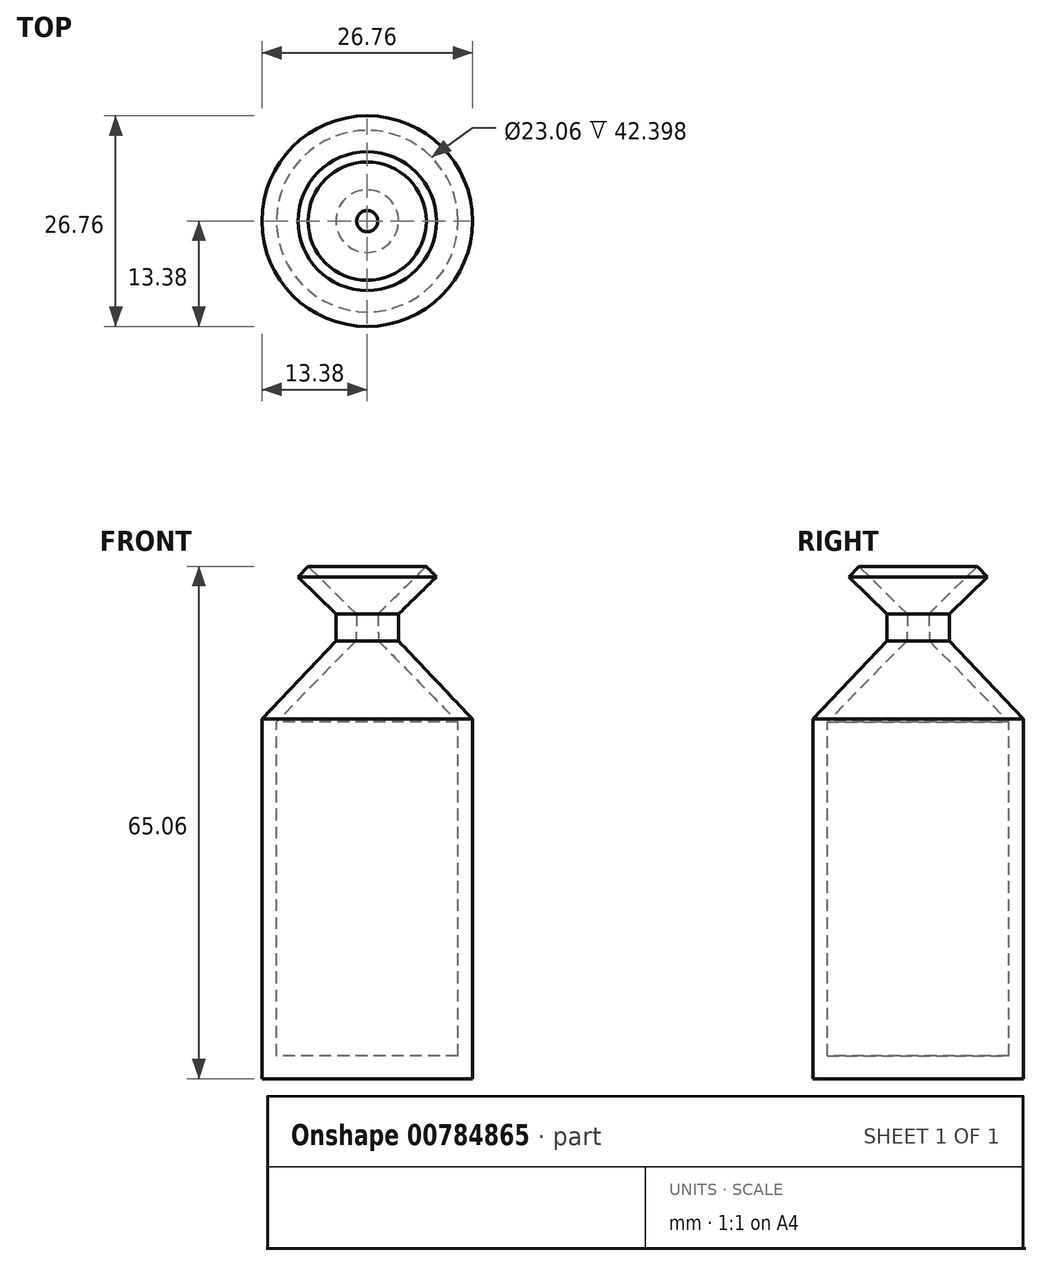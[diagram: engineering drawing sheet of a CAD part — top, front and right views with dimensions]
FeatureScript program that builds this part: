
annotation { "Feature Type Name" : "Feature", "Feature Type Description" : "" }
export const myFeature = defineFeature(function(context is Context, id is Id, definition is map)
    precondition{}
    {
        {
            var Q0;
            Q0=qCreatedBy(makeId("Front.planeOp"),FACE);
            var sketch = newSketch(context, id + "F0", { "sketchPlane" : qUnion([Q0])});
            skLineSegment(sketch, "E0", {"start": v(0, 0) * mm, "end": v(13.38, 0) * mm});
            skLineSegment(sketch, "E1", {"start": v(13.38, 0) * mm, "end": v(13.38, 45.67) * mm});
            skLineSegment(sketch, "E2", {"start": v(13.38, 45.67) * mm, "end": v(3.98, 55.62) * mm});
            skLineSegment(sketch, "E3", {"start": v(3.98, 55.62) * mm, "end": v(3.98, 59.03) * mm});
            skLineSegment(sketch, "E4", {"start": v(3.98, 59.03) * mm, "end": v(8.8, 63.74) * mm});
            skLineSegment(sketch, "E5", {"start": v(8.8, 63.74) * mm, "end": v(7.5, 65.06) * mm});
            skLineSegment(sketch, "E6", {"start": v(7.5, 65.06) * mm, "end": v(1.35, 59.03) * mm});
            skLineSegment(sketch, "E7", {"start": v(1.35, 59.03) * mm, "end": v(1.43, 55.62) * mm});
            skLineSegment(sketch, "E8", {"start": v(1.43, 55.62) * mm, "end": v(11.53, 45.3) * mm});
            skLineSegment(sketch, "E9", {"start": v(11.53, 45.3) * mm, "end": v(11.53, 2.9) * mm});
            skLineSegment(sketch, "E10", {"start": v(11.53, 2.9) * mm, "end": v(0, 2.9) * mm});
            skLineSegment(sketch, "E11", {"start": v(0, 2.9) * mm, "end": v(0, 0) * mm});
            skSolve(sketch);
        }
        {
            var Q0;
            Q0 = qSketchRegion(id + "F0", true);
            var Q1;
            Q1=sQuery(id+"F0.wireOp",EDGE,"E11");
            revolve(context, id + "F1", {"surfaceOperationType" : NewSurfaceOperationType.NEW, "entities" : qUnion([Q0]), "axis" : qUnion([Q1]), "revolveType" : RevolveType.FULL});
        }
    });
